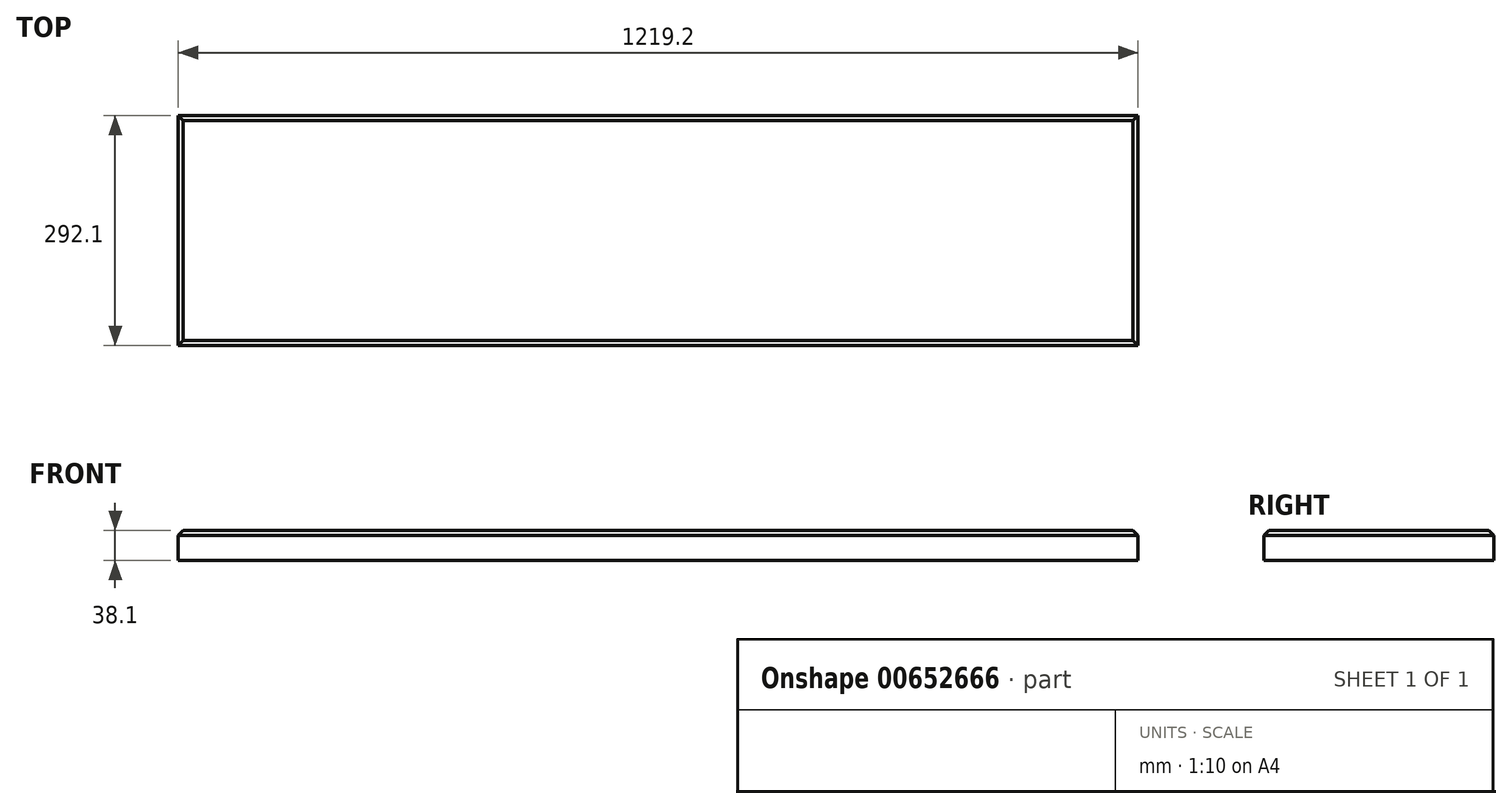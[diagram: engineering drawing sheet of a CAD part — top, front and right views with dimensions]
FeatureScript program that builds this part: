
annotation { "Feature Type Name" : "Feature", "Feature Type Description" : "" }
export const myFeature = defineFeature(function(context is Context, id is Id, definition is map)
    precondition{}
    {
        {
            var Q0;
            Q0=qCreatedBy(makeId("Top.planeOp"),FACE);
            var sketch = newSketch(context, id + "F0", { "sketchPlane" : qUnion([Q0])});
            skLineSegment(sketch, "E0.bottom", {"start": v(-609.6, -146.05) * mm, "end": v(609.6, -146.05) * mm});
            skLineSegment(sketch, "E0.top", {"start": v(-609.6, 146.05) * mm, "end": v(609.6, 146.05) * mm});
            skLineSegment(sketch, "E0.left", {"start": v(-609.6, -146.05) * mm, "end": v(-609.6, 146.05) * mm});
            skLineSegment(sketch, "E0.right", {"start": v(609.6, -146.05) * mm, "end": v(609.6, 146.05) * mm});
            skPoint(sketch, "E0.middle", {"position": v(0, 0) * mm});
            skSolve(sketch);
        }
        {
            var Q0;
            Q0=makeQuery(id+"F0.imprint","IMPRINT",FACE,{"disambiguationData":[TD([[makeQuery(id+"F0.imprint","IMPRINT",EDGE,{"derivedFrom":sQuery(id+"F0.wireOp",EDGE,"E0.bottom")}),1.0]])]});
            extrude(context, id + "F1", {"entities" : qUnion([Q0]), "depth" : 38.1 * mm, "offsetDistance" : 25.4 * mm});
        }
        {
            var Q0;
            Q0=makeQuery(id+"F1.opExtrude","CAP_EDGE",EDGE,{"disambiguationData":[OSD([sQuery(id+"F0.wireOp",EDGE,"E0.top")])],"isStart":false});
            var Q1;
            Q1=makeQuery(id+"F1.opExtrude","CAP_EDGE",EDGE,{"disambiguationData":[OSD([sQuery(id+"F0.wireOp",EDGE,"E0.right")])],"isStart":false});
            var Q2;
            Q2=makeQuery(id+"F1.opExtrude","CAP_EDGE",EDGE,{"disambiguationData":[OSD([sQuery(id+"F0.wireOp",EDGE,"E0.bottom")])],"isStart":false});
            var Q3;
            Q3=makeQuery(id+"F1.opExtrude","CAP_EDGE",EDGE,{"disambiguationData":[OSD([sQuery(id+"F0.wireOp",EDGE,"E0.left")])],"isStart":false});
            chamfer(context, id + "F2", {"entities" : qUnion([Q0, Q1, Q2, Q3]), "width" : 6.35 * mm, "tangentPropagation" : true});
        }
    });
